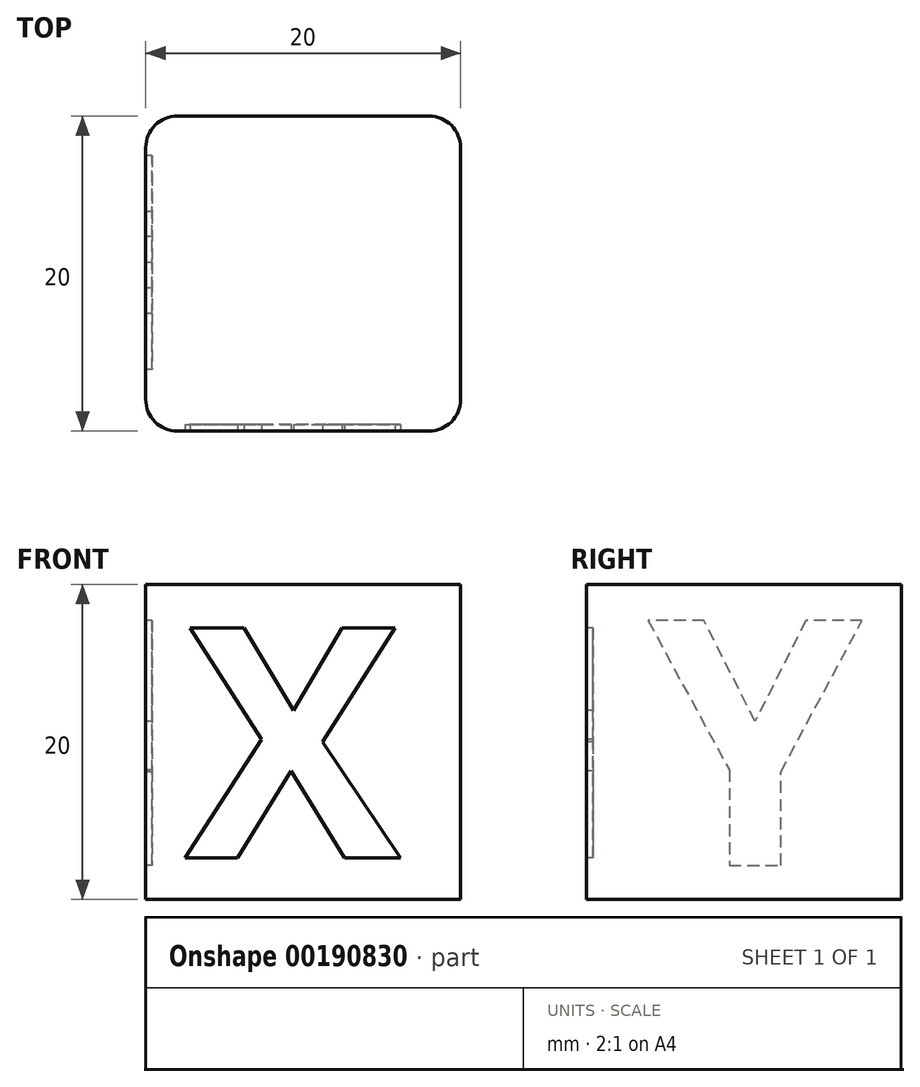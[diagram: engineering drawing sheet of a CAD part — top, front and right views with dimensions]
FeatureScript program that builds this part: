
annotation { "Feature Type Name" : "Feature", "Feature Type Description" : "" }
export const myFeature = defineFeature(function(context is Context, id is Id, definition is map)
    precondition{}
    {
        {
            var Q0;
            Q0=qCreatedBy(makeId("Top.planeOp"),FACE);
            var sketch = newSketch(context, id + "F0", { "sketchPlane" : qUnion([Q0])});
            skLineSegment(sketch, "E0.bottom", {"start": v(-10, 10) * mm, "end": v(10, 10) * mm});
            skLineSegment(sketch, "E0.top", {"start": v(-10, -10) * mm, "end": v(10, -10) * mm});
            skLineSegment(sketch, "E0.left", {"start": v(-10, 10) * mm, "end": v(-10, -10) * mm});
            skLineSegment(sketch, "E0.right", {"start": v(10, 10) * mm, "end": v(10, -10) * mm});
            skPoint(sketch, "E0.middle", {"position": v(0, 0) * mm});
            skSolve(sketch);
        }
        {
            var Q0;
            Q0=makeQuery(id+"F0.imprint","IMPRINT",FACE,{"disambiguationData":[TD([[makeQuery(id+"F0.imprint","IMPRINT",EDGE,{"derivedFrom":sQuery(id+"F0.wireOp",EDGE,"E0.bottom")}),-1.0]])]});
            extrude(context, id + "F1", {"entities" : qUnion([Q0]), "depth" : 20 * mm, "offsetDistance" : 25 * mm});
        }
        {
            var Q0;
            Q0=makeQuery(id+"F1.opExtrude","SWEPT_FACE",FACE,{"disambiguationData":[OSD([sQuery(id+"F0.wireOp",EDGE,"E0.top")])]});
            var sketch = newSketch(context, id + "F2", { "sketchPlane" : qUnion([Q0])});
            skPoint(sketch, "E1.middle", {"position": v(0, 10) * mm});
            skPoint(sketch, "E2", {"position": v(-10, 10) * mm});
            skText(sketch, "E3", { "text": "X", "fontName": "OpenSans-Bold.ttf"});
            skPoint(sketch, "E1.right.start.orphan", {"position": v(7.5, 17.5) * mm});
            skPoint(sketch, "E1.top.end.orphan", {"position": v(7.5, 2.5) * mm});
            skPoint(sketch, "E1.left.end.orphan", {"position": v(-7.5, 2.5) * mm});
            skPoint(sketch, "E1.left.start.orphan", {"position": v(-7.5, 17.5) * mm});
            const initialGuessF2  = {"E3": [-0.0075, 0.00262, 1, 0, 0.01476]};
            skSetInitialGuess(sketch, initialGuessF2);
            skSolve(sketch);
        }
        {
            var Q0;
            Q0=makeQuery(id+"F1.opExtrude","SWEPT_FACE",FACE,{"disambiguationData":[OSD([sQuery(id+"F0.wireOp",EDGE,"E0.left")])]});
            var sketch = newSketch(context, id + "F3", { "sketchPlane" : qUnion([Q0])});
            skText(sketch, "E4", { "text": "Y", "fontName": "OpenSans-Bold.ttf"});
            skPoint(sketch, "E5", {"position": v(0, 10) * mm});
            skPoint(sketch, "E6", {"position": v(0, 20) * mm});
            skPoint(sketch, "E7", {"position": v(10, 10) * mm});
            const initialGuessF3  = {"E4": [-0.0075, 0.00216, 1, 0, 0.01568]};
            skSetInitialGuess(sketch, initialGuessF3);
            skSolve(sketch);
        }
        {
            var Q0;
            Q0=makeQuery(id+"F3.imprint","IMPRINT",FACE,{"disambiguationData":[TD([[makeQuery(id+"F3.imprint","IMPRINT",EDGE,{"derivedFrom":sQuery(id+"F3.wireOp",EDGE,"E4.sketch_text.stroke-0")}),-1.0]])]});
            extrude(context, id + "F4", {"entities" : qUnion([Q0]), "operationType" : NewBodyOperationType.REMOVE, "oppositeDirection" : true, "depth" : 0.4 * mm, "offsetDistance" : 25 * mm});
        }
        {
            var Q0;
            Q0=makeQuery(id+"F2.imprint","IMPRINT",FACE,{"disambiguationData":[TD([[makeQuery(id+"F2.imprint","IMPRINT",EDGE,{"derivedFrom":sQuery(id+"F2.wireOp",EDGE,"E3.sketch_text.stroke-0")}),-1.0]])]});
            extrude(context, id + "F5", {"entities" : qUnion([Q0]), "operationType" : NewBodyOperationType.REMOVE, "oppositeDirection" : true, "depth" : 0.4 * mm, "offsetDistance" : 25 * mm});
        }
        {
            var Q0;
            Q0=makeQuery(id+"F1.opExtrude","SWEPT_EDGE",EDGE,{"disambiguationData":[OSD([sQuery(id+"F0.wireOp",EDGE,"E0.top"),sQuery(id+"F0.wireOp",EDGE,"E0.left")])]});
            var Q1;
            Q1=makeQuery(id+"F1.opExtrude","SWEPT_EDGE",EDGE,{"disambiguationData":[OSD([sQuery(id+"F0.wireOp",EDGE,"E0.bottom"),sQuery(id+"F0.wireOp",EDGE,"E0.left")])]});
            var Q2;
            Q2=makeQuery(id+"F1.opExtrude","SWEPT_EDGE",EDGE,{"disambiguationData":[OSD([sQuery(id+"F0.wireOp",EDGE,"E0.top"),sQuery(id+"F0.wireOp",EDGE,"E0.right")])]});
            var Q3;
            Q3=makeQuery(id+"F1.opExtrude","SWEPT_EDGE",EDGE,{"disambiguationData":[OSD([sQuery(id+"F0.wireOp",EDGE,"E0.bottom"),sQuery(id+"F0.wireOp",EDGE,"E0.right")])]});
            fillet(context, id + "F6", {"entities" : qUnion([Q0, Q1, Q2, Q3]), "tangentPropagation" : true, "radius" : 2 * mm, "defaultsChanged" : true, "vertexSettings" : [], "allowEdgeOverflow" : false});
        }
    });
